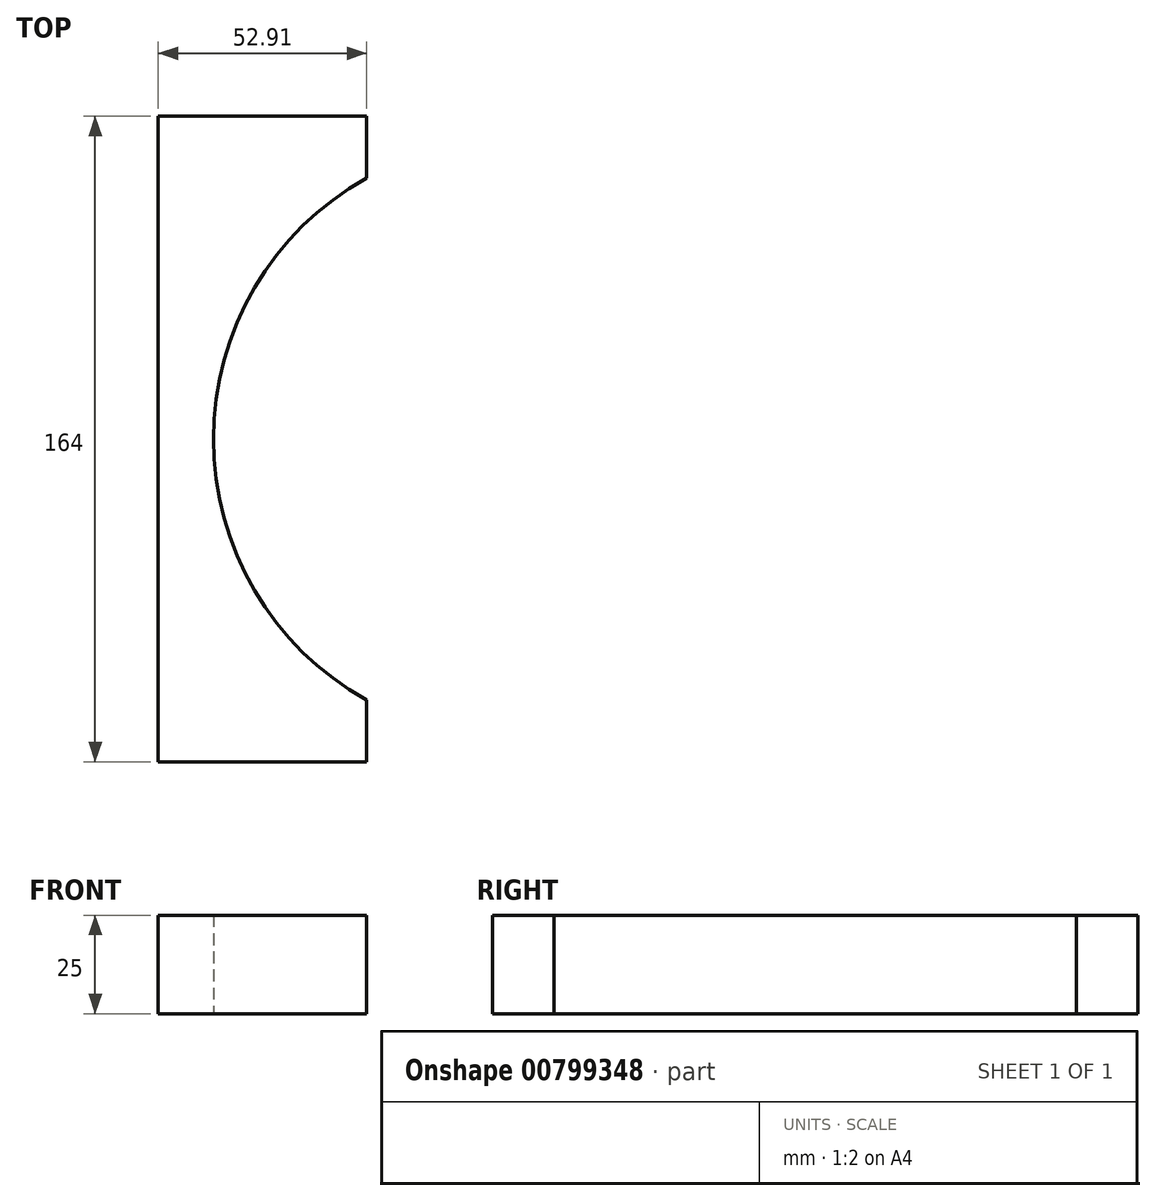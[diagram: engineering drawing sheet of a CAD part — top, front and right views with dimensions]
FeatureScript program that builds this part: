
annotation { "Feature Type Name" : "Feature", "Feature Type Description" : "" }
export const myFeature = defineFeature(function(context is Context, id is Id, definition is map)
    precondition{}
    {
        {
            var Q0;
            Q0=qCreatedBy(makeId("Top.planeOp"),FACE);
            var sketch = newSketch(context, id + "F0", { "sketchPlane" : qUnion([Q0])});
            skArc(sketch, "E0", {"start": v(0, 76) * mm, "mid": v(-76, 0) * mm, "end": v(0, -76) * mm});
            skArc(sketch, "E1", {"start": v(0, 90) * mm, "mid": v(-4, 89.91) * mm, "end": v(-8, 89.64) * mm});
            skLineSegment(sketch, "E2", {"start": v(0, 0) * mm, "end": v(0, 90) * mm});
            skLineSegment(sketch, "E3", {"start": v(0, 90) * mm, "end": v(0, 76) * mm});
            skLineSegment(sketch, "E4", {"start": v(-8, 82) * mm, "end": v(-37.1, 82) * mm});
            skLineSegment(sketch, "E5", {"start": v(-8, -82) * mm, "end": v(-37.1, -82) * mm});
            skLineSegment(sketch, "E6", {"start": v(-8, 82) * mm, "end": v(-8, 89.64) * mm});
            skLineSegment(sketch, "E7", {"start": v(-8, -82) * mm, "end": v(-8, -89.64) * mm});
            skLineSegment(sketch, "E8.trimOffspring", {"start": v(0, 0) * mm, "end": v(0, -90) * mm});
            skArc(sketch, "E9.trimOffspring", {"start": v(-37.1, 82) * mm, "mid": v(-90, 0) * mm, "end": v(-37.1, -82) * mm});
            skArc(sketch, "E10.trimOffspring", {"start": v(-8, -89.64) * mm, "mid": v(-4, -89.91) * mm, "end": v(0, -90) * mm});
            skLineSegment(sketch, "E11", {"start": v(-37.1, 82) * mm, "end": v(-37.1, -82) * mm});
            skPoint(sketch, "E12.oppositeSnap0", {"position": v(-90, 0) * mm});
            skLineSegment(sketch, "E12.bottom", {"start": v(-37.1, 82) * mm, "end": v(-90, 82) * mm});
            skLineSegment(sketch, "E12.top", {"start": v(-37.1, -82) * mm, "end": v(-90, -82) * mm});
            skLineSegment(sketch, "E12.right", {"start": v(-90, 82) * mm, "end": v(-90, -82) * mm});
            skSolve(sketch);
        }
        {
            var Q0;
            {var subQ4=sQuery(id+"F0.wireOp",EDGE,"E9.trimOffspring");Q0=makeQuery(id+"F0.imprint","IMPRINT",FACE,{"disambiguationData":[TD([[makeQuery(id+"F0.imprint","IMPRINT",EDGE,{"derivedFrom":subQ4}),1.0]])]});}
            var Q1;
            {var subQ0=sQuery(id+"F0.wireOp",EDGE,"E12.bottom");Q1=makeQuery(id+"F0.imprint","IMPRINT",FACE,{"disambiguationData":[TD([[makeQuery(id+"F0.imprint","IMPRINT",EDGE,{"derivedFrom":subQ0}),1.0]])]});}
            var Q2;
            {var subQ0=sQuery(id+"F0.wireOp",EDGE,"E12.top");Q2=makeQuery(id+"F0.imprint","IMPRINT",FACE,{"disambiguationData":[TD([[makeQuery(id+"F0.imprint","IMPRINT",EDGE,{"derivedFrom":subQ0}),-1.0]])]});}
            extrude(context, id + "F1", {"entities" : qUnion([Q0, Q1, Q2]), "depth" : 25 * mm, "offsetDistance" : 25 * mm});
        }
    });
